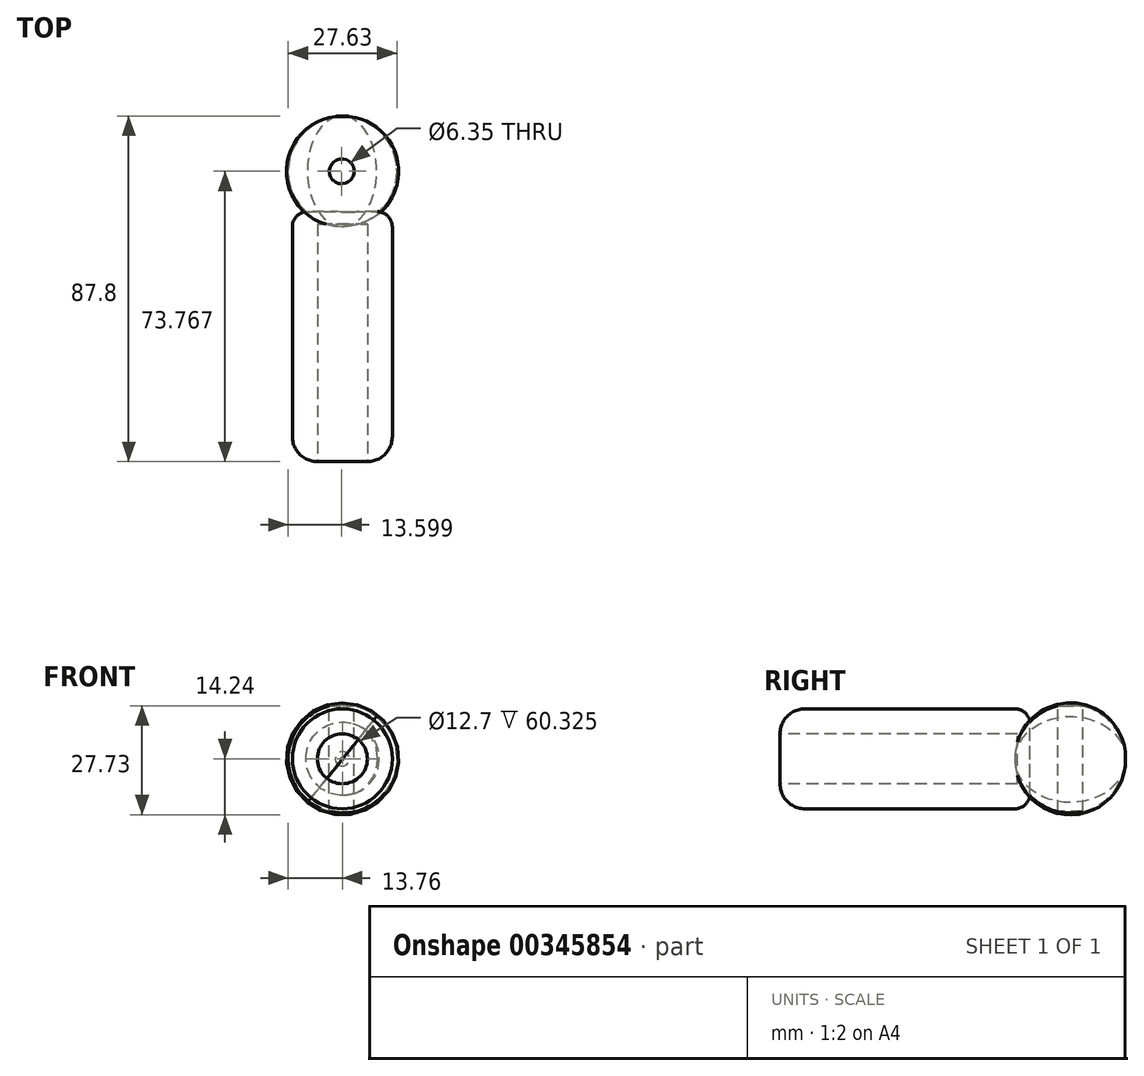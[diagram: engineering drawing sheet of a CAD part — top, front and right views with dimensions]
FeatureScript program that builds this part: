
annotation { "Feature Type Name" : "Feature", "Feature Type Description" : "" }
export const myFeature = defineFeature(function(context is Context, id is Id, definition is map)
    precondition{}
    {
        {
            var Q0;
            Q0=qCreatedBy(makeId("Front.planeOp"),FACE);
            var sketch = newSketch(context, id + "F6", { "sketchPlane" : qUnion([Q0])});
            skCircle(sketch, "E0", {"center": v(0, 0) * mm, "radius": 12.7 * mm});
            skSolve(sketch);
        }
        {
            var Q0;
            Q0=makeQuery(id+"F6.imprint","IMPRINT",FACE,{"disambiguationData":[TD([[makeQuery(id+"F6.imprint","IMPRINT",EDGE,{"derivedFrom":sQuery(id+"F6.wireOp",EDGE,"E0")}),1.0]])]});
            extrude(context, id + "F0", {"entities" : qUnion([Q0]), "depth" : 63.5 * mm});
        }
        {
            var Q0;
            Q0=makeQuery(id+"F0.opExtrude","CAP_EDGE",EDGE,{"disambiguationData":[OSD([sQuery(id+"F6.wireOp",EDGE,"E0")])],"isStart":false});
            fillet(context, id + "F1", {"entities" : qUnion([Q0]), "radius" : 6.35 * mm, "tangentPropagation" : true, "allowEdgeOverflow" : false});
        }
        {
            var Q0;
            Q0=makeQuery(id+"F0.opExtrude","CAP_EDGE",EDGE,{"disambiguationData":[OSD([sQuery(id+"F6.wireOp",EDGE,"E0")])],"isStart":true});
            fillet(context, id + "F2", {"entities" : qUnion([Q0]), "radius" : 3.8 * mm, "tangentPropagation" : true, "allowEdgeOverflow" : false});
        }
        {
            var Q0;
            Q0=qCreatedBy(makeId("Top.planeOp"),FACE);
            var sketch = newSketch(context, id + "F3", { "sketchPlane" : qUnion([Q0])});
            skArc(sketch, "E1", {"start": v(9.4, 0) * mm, "mid": v(-0.16, 24.3) * mm, "end": v(-9.72, 0) * mm});
            skPoint(sketch, "E2.start.orphan", {"position": v(-9.72, 0) * mm});
            skLineSegment(sketch, "E3", {"start": v(9.4, 0) * mm, "end": v(0, 0) * mm});
            skPoint(sketch, "E4", {"position": v(0, 24.3) * mm});
            skPoint(sketch, "E4.positionSnap0", {"position": v(-0.16, 24.3) * mm});
            skLineSegment(sketch, "E5", {"start": v(0.1, -0.04) * mm, "end": v(0, 24.3) * mm});
            skSolve(sketch);
        }
        {
            var Q0;
            {var subQ0=sQuery(id+"F3.wireOp",EDGE,"E3");var subQ1=sQuery(id+"F3.wireOp",EDGE,"E1");var subQ2=makeQuery(id+"F3.imprint","INTERSECT",VERTEX,{"derivedFrom":[subQ1,subQ0]});Q0=makeQuery(id+"F3.imprint","IMPRINT",FACE,{"disambiguationData":[TD([[makeQuery(id+"F3.imprint","IMPRINT",EDGE,{"disambiguationData":[TD([[subQ2,-1.0]])],"derivedFrom":subQ1}),1.0]])]});}
            var Q1;
            Q1=sQuery(id+"F3.wireOp",EDGE,"E5");
            revolve(context, id + "F4", {"operationType" : NewBodyOperationType.ADD, "entities" : qUnion([Q0]), "axis" : qUnion([Q1]), "revolveType" : RevolveType.FULL});
        }
        {
            var Q0;
            Q0=sQuery(id+"F3.wireOp",VERTEX,"E1.center");
            var Q1;
            Q1=makeQuery(id+"F0.opExtrude","SWEPT_BODY",BODY,{"disambiguationData":[OSD([sQuery(id+"F6.wireOp",EDGE,"E0")])]});
            hole(context, id + "F5", {"style" : HoleStyle.SIMPLE, "endStyle" : HoleEndStyle.THROUGH, "holeDiameter" : 6.35 * mm, "locations" : qUnion([Q0]), "scope" : qUnion([Q1]), "isTappedThrough" : true});
        }
        {
            var Q0;
            Q0=sQuery(id+"F3.wireOp",VERTEX,"E1.center");
            var Q1;
            Q1=makeQuery(id+"F0.opExtrude","SWEPT_BODY",BODY,{"disambiguationData":[OSD([sQuery(id+"F6.wireOp",EDGE,"E0")])]});
            var Q2;
            Q2=makeQuery(id+"F0.opExtrude","SWEPT_BODY",BODY,{"disambiguationData":[OSD([sQuery(id+"F6.wireOp",EDGE,"E0")])]});
            hole(context, id + "F7", {"style" : HoleStyle.SIMPLE, "endStyle" : HoleEndStyle.THROUGH, "oppositeDirection" : true, "holeDiameter" : 6.35 * mm, "locations" : qUnion([Q0]), "scope" : qUnion([Q1, Q2]), "isTappedThrough" : true});
        }
        {
            var Q0;
            Q0=makeQuery(id+"F0.opExtrude","CAP_FACE",FACE,{"disambiguationData":[OSD([sQuery(id+"F6.wireOp",EDGE,"E0")])],"isStart":false});
            extrude(context, id + "F8", {"entities" : qUnion([Q0]), "operationType" : NewBodyOperationType.REMOVE, "oppositeDirection" : true, "depth" : 60.32 * mm});
        }
    });
